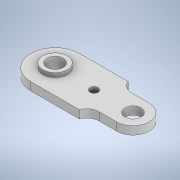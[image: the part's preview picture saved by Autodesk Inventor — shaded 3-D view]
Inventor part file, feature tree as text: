
AUTODESK INVENTOR PART (.ipt)
format: ipt  version: 2022.2 (Build 262287030, 287C)  size: 132,608 bytes
history: native  units: in
note: dims shown in document units (in); Inventor stores cm internally (conversion verified against a paired STEP export)
features: sketch x2, hole x2, extrude x1, emboss x1
ambient origin geometry x8: Origin, YZ Plane, XZ Plane, XY Plane, X Axis, Y Axis, Z Axis, Center Point
bodies: Solid1 (feature_tree)
feature tree (6):
  sketch  "Sketch1"  dims[d1=1.1811in d2=1.8898in]
  extrude  "Extrusion1"  Depth=1.1811in
  hole  "Hole2"  [1 undecoded]
  hole  "Hole3"  [1 undecoded]
  emboss  "Emboss1"
  sketch  "Sketch3"  dims[d3=2.3622in d4=0.5906in d5=0.7874in d6=3.7795in d7=0.3937in d8=0.0in d16=0.7874in d17=0.2362in d18=0.1575in d19=0.0787in d20=90.0deg d21=0.315in d22=0.8108in d23=0.3937in d24=0.2362in d25=0.1575in d26=0.0787in d27=90.0deg d28=0.315in d29=0.8108in d30=1.1811in d31=0.1969in d32=0.0in]
note: 2 required parameter values undecoded (feature->parameter linkage not recoverable at this tier; creation-order binding heuristic only, values carry confidence <= 0.55)
